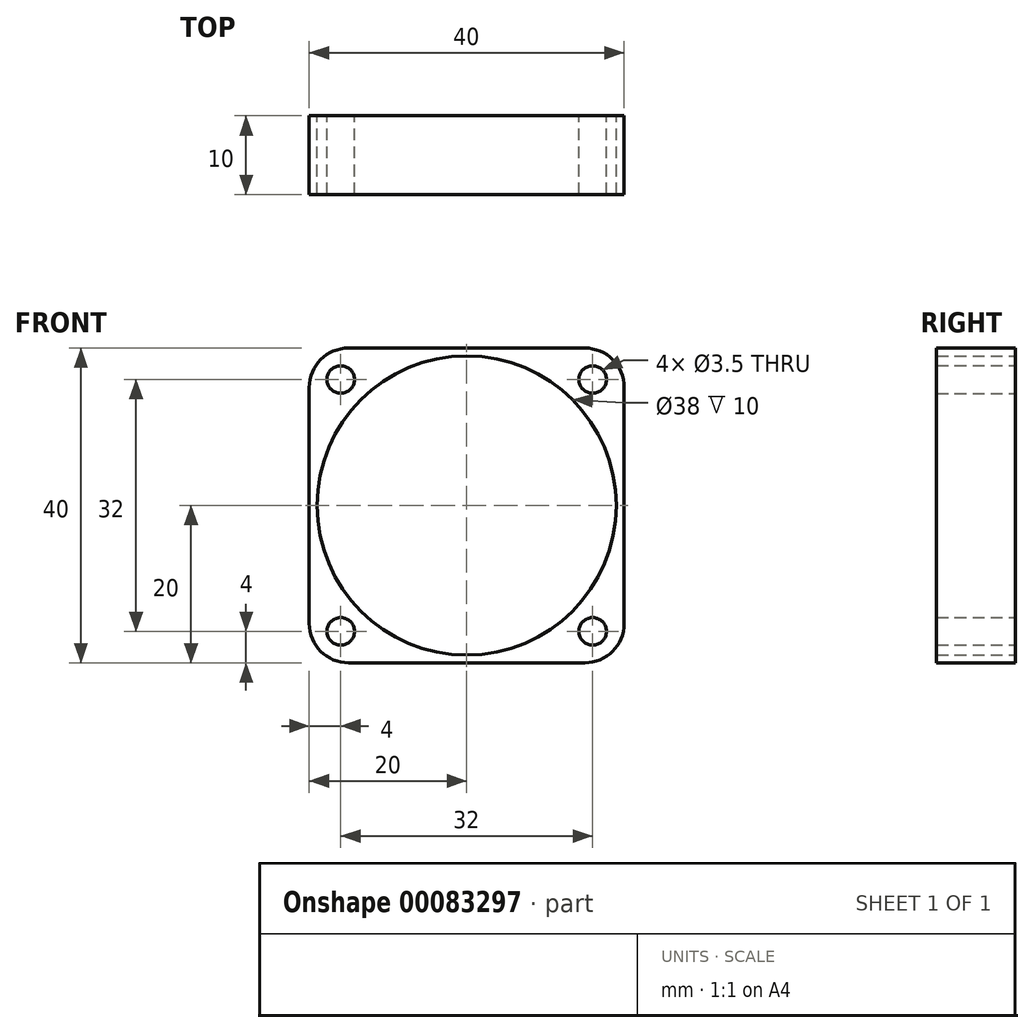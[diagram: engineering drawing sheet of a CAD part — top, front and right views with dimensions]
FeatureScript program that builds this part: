
annotation { "Feature Type Name" : "Feature", "Feature Type Description" : "" }
export const myFeature = defineFeature(function(context is Context, id is Id, definition is map)
    precondition{}
    {
        {
            var Q0;
            Q0=qCreatedBy(makeId("Front.planeOp"),FACE);
            var sketch = newSketch(context, id + "F0", { "sketchPlane" : qUnion([Q0])});
            skLineSegment(sketch, "E0.bottom", {"start": v(20, 20) * mm, "end": v(-20, 20) * mm});
            skLineSegment(sketch, "E0.top", {"start": v(20, -20) * mm, "end": v(-20, -20) * mm});
            skLineSegment(sketch, "E0.left", {"start": v(20, 20) * mm, "end": v(20, -20) * mm});
            skLineSegment(sketch, "E0.right", {"start": v(-20, 20) * mm, "end": v(-20, -20) * mm});
            skPoint(sketch, "E0.middle", {"position": v(0, 0) * mm});
            skCircle(sketch, "E1", {"center": v(0, 0) * mm, "radius": 19 * mm});
            skLineSegment(sketch, "E2.bottom", {"start": v(16, 16) * mm, "end": v(-16, 16) * mm, "construction": true});
            skLineSegment(sketch, "E2.top", {"start": v(16, -16) * mm, "end": v(-16, -16) * mm, "construction": true});
            skLineSegment(sketch, "E2.left", {"start": v(16, 16) * mm, "end": v(16, -16) * mm, "construction": true});
            skLineSegment(sketch, "E2.right", {"start": v(-16, 16) * mm, "end": v(-16, -16) * mm, "construction": true});
            skCircle(sketch, "E3", {"center": v(-16, -16) * mm, "radius": 1.75 * mm});
            skCircle(sketch, "E4", {"center": v(-16, 16) * mm, "radius": 1.75 * mm});
            skCircle(sketch, "E5", {"center": v(16, 16) * mm, "radius": 1.75 * mm});
            skCircle(sketch, "E6", {"center": v(16, -16) * mm, "radius": 1.75 * mm});
            skSolve(sketch);
        }
        {
            var Q0;
            Q0=qSketchRegion(id+"F0",true);
            extrude(context, id + "F1", {"entities" : qUnion([Q0]), "depth" : 10 * mm});
        }
        {
            var Q0;
            Q0=makeQuery(id+"F1.opExtrude","SWEPT_EDGE",EDGE,{"disambiguationData":[OSD([sQuery(id+"F0.wireOp",EDGE,"E0.bottom"),sQuery(id+"F0.wireOp",EDGE,"E0.right")])]});
            var Q1;
            Q1=makeQuery(id+"F1.opExtrude","SWEPT_EDGE",EDGE,{"disambiguationData":[OSD([sQuery(id+"F0.wireOp",EDGE,"E0.bottom"),sQuery(id+"F0.wireOp",EDGE,"E0.left")])]});
            var Q2;
            Q2=makeQuery(id+"F1.opExtrude","SWEPT_EDGE",EDGE,{"disambiguationData":[OSD([sQuery(id+"F0.wireOp",EDGE,"E0.top"),sQuery(id+"F0.wireOp",EDGE,"E0.left")])]});
            var Q3;
            Q3=makeQuery(id+"F1.opExtrude","SWEPT_EDGE",EDGE,{"disambiguationData":[OSD([sQuery(id+"F0.wireOp",EDGE,"E0.top"),sQuery(id+"F0.wireOp",EDGE,"E0.right")])]});
            fillet(context, id + "F2", {"entities" : qUnion([Q0, Q1, Q2, Q3]), "radius" : 5 * mm, "tangentPropagation" : true, "allowEdgeOverflow" : false});
        }
    });
